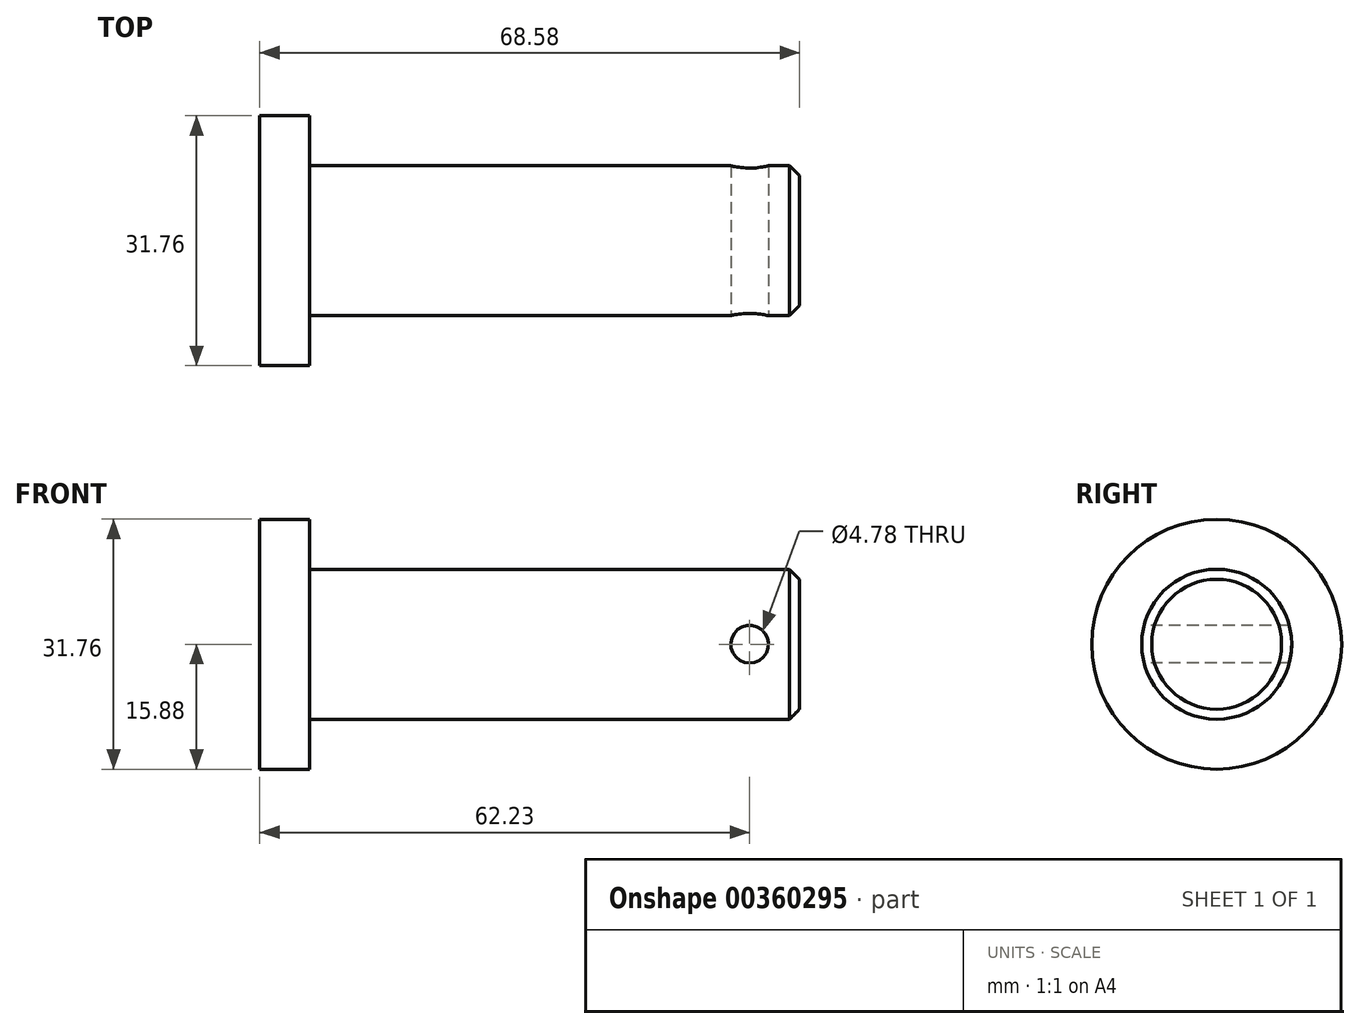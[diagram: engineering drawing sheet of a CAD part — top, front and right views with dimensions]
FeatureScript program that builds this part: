
annotation { "Feature Type Name" : "Feature", "Feature Type Description" : "" }
export const myFeature = defineFeature(function(context is Context, id is Id, definition is map)
    precondition{}
    {
        {
            var Q0;
            Q0=qCreatedBy(makeId("Right.planeOp"),FACE);
            var sketch = newSketch(context, id + "F0", { "sketchPlane" : qUnion([Q0])});
            skCircle(sketch, "E0", {"center": v(0, 0) * mm, "radius": 15.88 * mm});
            skSolve(sketch);
        }
        {
            var Q0;
            Q0 = qSketchRegion(id + "F0", true);
            extrude(context, id + "F1", {"entities" : qUnion([Q0]), "depth" : 6.35 * mm});
        }
        {
            var Q0;
            Q0=makeQuery(id+"F1.opExtrude","CAP_FACE",FACE,{"disambiguationData":[OSD([sQuery(id+"F0.wireOp",EDGE,"E0")])],"isStart":false});
            var sketch = newSketch(context, id + "F2", { "sketchPlane" : qUnion([Q0])});
            skCircle(sketch, "E1", {"center": v(0, 0) * mm, "radius": 9.53 * mm});
            skSolve(sketch);
        }
        {
            var Q0;
            Q0 = qSketchRegion(id + "F2", true);
            extrude(context, id + "F3", {"entities" : qUnion([Q0]), "operationType" : NewBodyOperationType.ADD, "depth" : 62.23 * mm});
        }
        {
            var Q0;
            Q0=makeQuery(id+"F3.opExtrude","CAP_EDGE",EDGE,{"disambiguationData":[OSD([sQuery(id+"F2.wireOp",EDGE,"E1")])],"isStart":false});
            chamfer(context, id + "F4", {"entities" : qUnion([Q0]), "chamferType" : ChamferType.OFFSET_ANGLE, "width" : 1.27 * mm, "oppositeDirection" : false, "angle" : 45 * degree, "tangentPropagation" : true});
        }
        {
            var Q0;
            Q0=qCreatedBy(makeId("Front.planeOp"),FACE);
            var sketch = newSketch(context, id + "F5", { "sketchPlane" : qUnion([Q0])});
            skCircle(sketch, "E2", {"center": v(62.23, 0) * mm, "radius": 2.39 * mm});
            skSolve(sketch);
        }
        {
            var Q0;
            Q0 = qSketchRegion(id + "F5", true);
            extrude(context, id + "F6", {"entities" : qUnion([Q0]), "operationType" : NewBodyOperationType.REMOVE, "oppositeDirection" : true, "depth" : 25.4 * mm, "hasSecondDirection" : true, "secondDirectionOppositeDirection" : false, "secondDirectionDepth" : 25.4 * mm});
        }
    });
